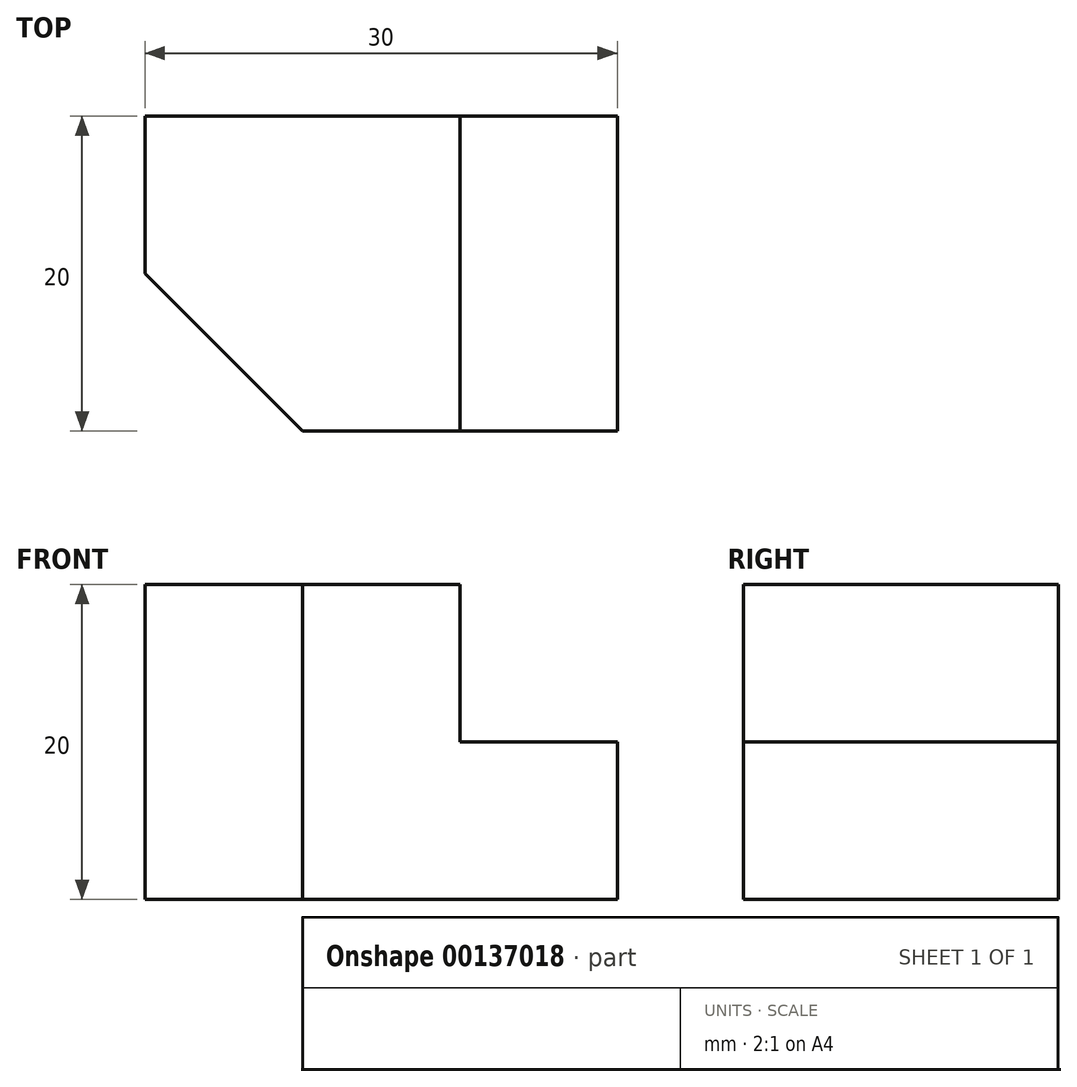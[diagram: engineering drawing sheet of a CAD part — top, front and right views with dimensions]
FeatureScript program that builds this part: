
annotation { "Feature Type Name" : "Feature", "Feature Type Description" : "" }
export const myFeature = defineFeature(function(context is Context, id is Id, definition is map)
    precondition{}
    {
        {
            var Q0;
            Q0=qCreatedBy(makeId("Top.planeOp"),FACE);
            var sketch = newSketch(context, id + "F0", { "sketchPlane" : qUnion([Q0])});
            skLineSegment(sketch, "E0", {"start": v(0, 0) * mm, "end": v(-10, 10) * mm});
            skLineSegment(sketch, "E1", {"start": v(-10, 10) * mm, "end": v(-10, 20) * mm});
            skLineSegment(sketch, "E2", {"start": v(-10, 20) * mm, "end": v(20, 20) * mm});
            skLineSegment(sketch, "E3", {"start": v(20, 20) * mm, "end": v(20, 0) * mm});
            skLineSegment(sketch, "E4", {"start": v(20, 0) * mm, "end": v(0, 0) * mm});
            skSolve(sketch);
        }
        {
            var Q0;
            Q0 = qSketchRegion(id + "F0", true);
            extrude(context, id + "F1", {"entities" : qUnion([Q0]), "depth" : 20 * mm});
        }
        {
            var Q0;
            Q0=makeQuery(id+"F1.opExtrude","SWEPT_FACE",FACE,{"disambiguationData":[OSD([sQuery(id+"F0.wireOp",EDGE,"E4")])]});
            var sketch = newSketch(context, id + "F2", { "sketchPlane" : qUnion([Q0])});
            skLineSegment(sketch, "E5", {"start": v(10, 20) * mm, "end": v(10, 10) * mm});
            skPoint(sketch, "E5.endSnap0", {"position": v(20, 10) * mm});
            skLineSegment(sketch, "E6", {"start": v(10, 10) * mm, "end": v(20, 10) * mm});
            skLineSegment(sketch, "E7", {"start": v(20, 20) * mm, "end": v(20, 10) * mm});
            skLineSegment(sketch, "E8", {"start": v(20, 20) * mm, "end": v(10, 20) * mm});
            skSolve(sketch);
        }
        {
            var Q0;
            Q0 = qSketchRegion(id + "F2", true);
            extrude(context, id + "F3", {"entities" : qUnion([Q0]), "operationType" : NewBodyOperationType.REMOVE, "endBound" : BoundingType.THROUGH_ALL, "oppositeDirection" : true, "depth" : 25 * mm});
        }
    });
